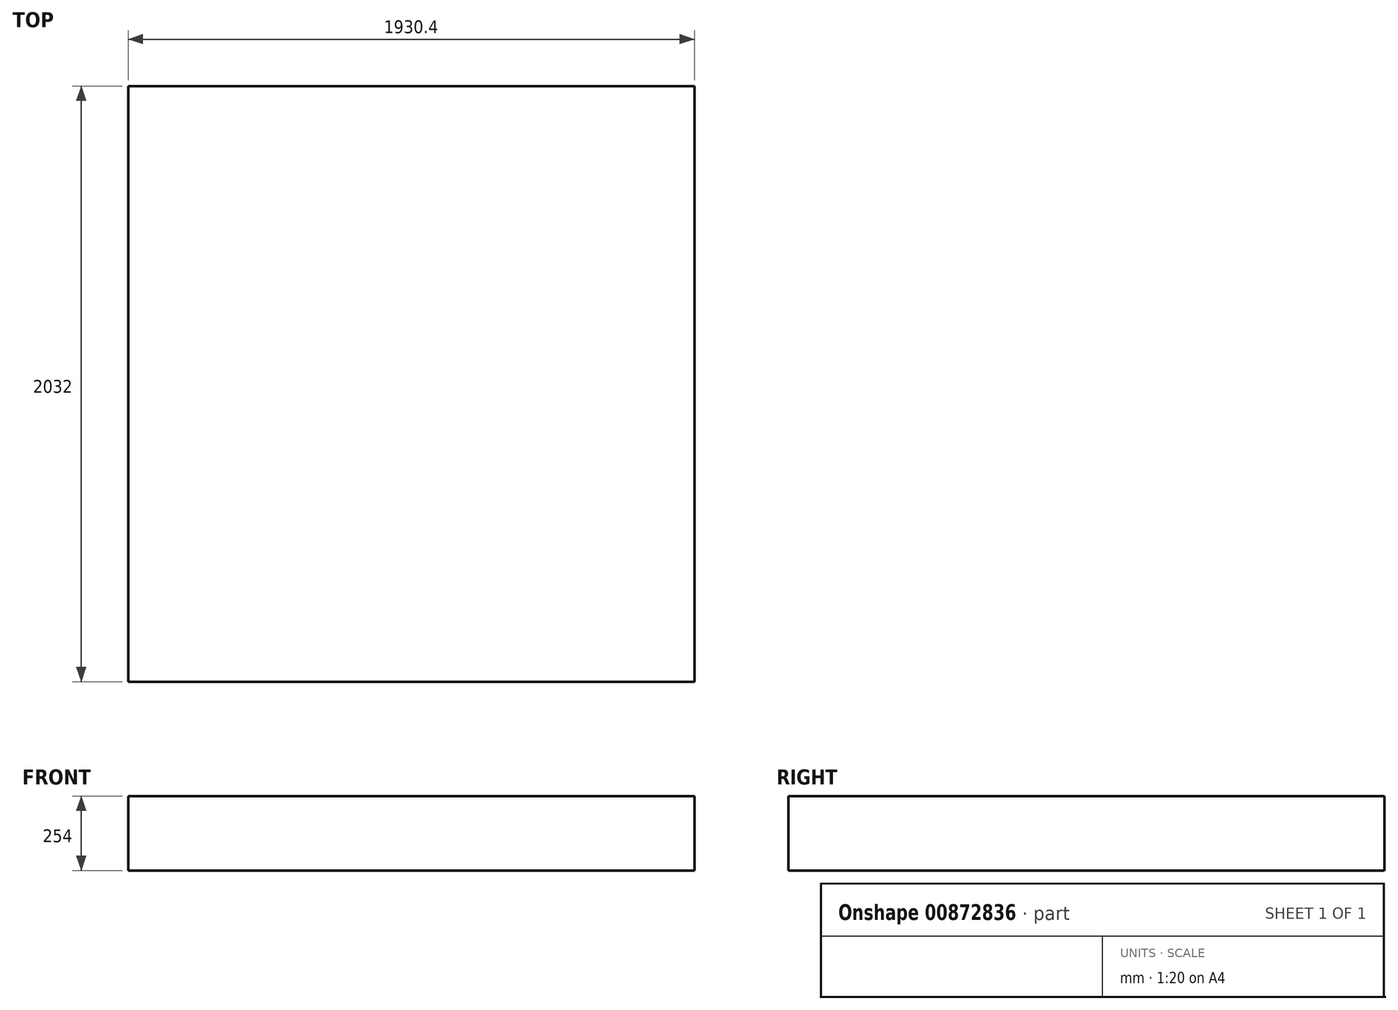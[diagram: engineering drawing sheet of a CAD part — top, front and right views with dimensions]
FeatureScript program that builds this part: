
annotation { "Feature Type Name" : "Feature", "Feature Type Description" : "" }
export const myFeature = defineFeature(function(context is Context, id is Id, definition is map)
    precondition{}
    {
        {
            var Q0;
            Q0=qCreatedBy(makeId("Top.planeOp"),FACE);
            var sketch = newSketch(context, id + "F0", { "sketchPlane" : qUnion([Q0])});
            skLineSegment(sketch, "E0.bottom", {"start": v(965.2, -1016) * mm, "end": v(-965.2, -1016) * mm});
            skLineSegment(sketch, "E0.top", {"start": v(965.2, 1016) * mm, "end": v(-965.2, 1016) * mm});
            skLineSegment(sketch, "E0.left", {"start": v(965.2, -1016) * mm, "end": v(965.2, 1016) * mm});
            skLineSegment(sketch, "E0.right", {"start": v(-965.2, -1016) * mm, "end": v(-965.2, 1016) * mm});
            skPoint(sketch, "E0.middle", {"position": v(0, 0) * mm});
            skSolve(sketch);
        }
        {
            var Q0;
            Q0=makeQuery(id+"F0.imprint","IMPRINT",FACE,{"disambiguationData":[TD([[makeQuery(id+"F0.imprint","IMPRINT",EDGE,{"derivedFrom":sQuery(id+"F0.wireOp",EDGE,"E0.bottom")}),-1.0]])]});
            extrude(context, id + "F1", {"entities" : qUnion([Q0]), "depth" : 254 * mm, "offsetDistance" : 25.4 * mm});
        }
    });
